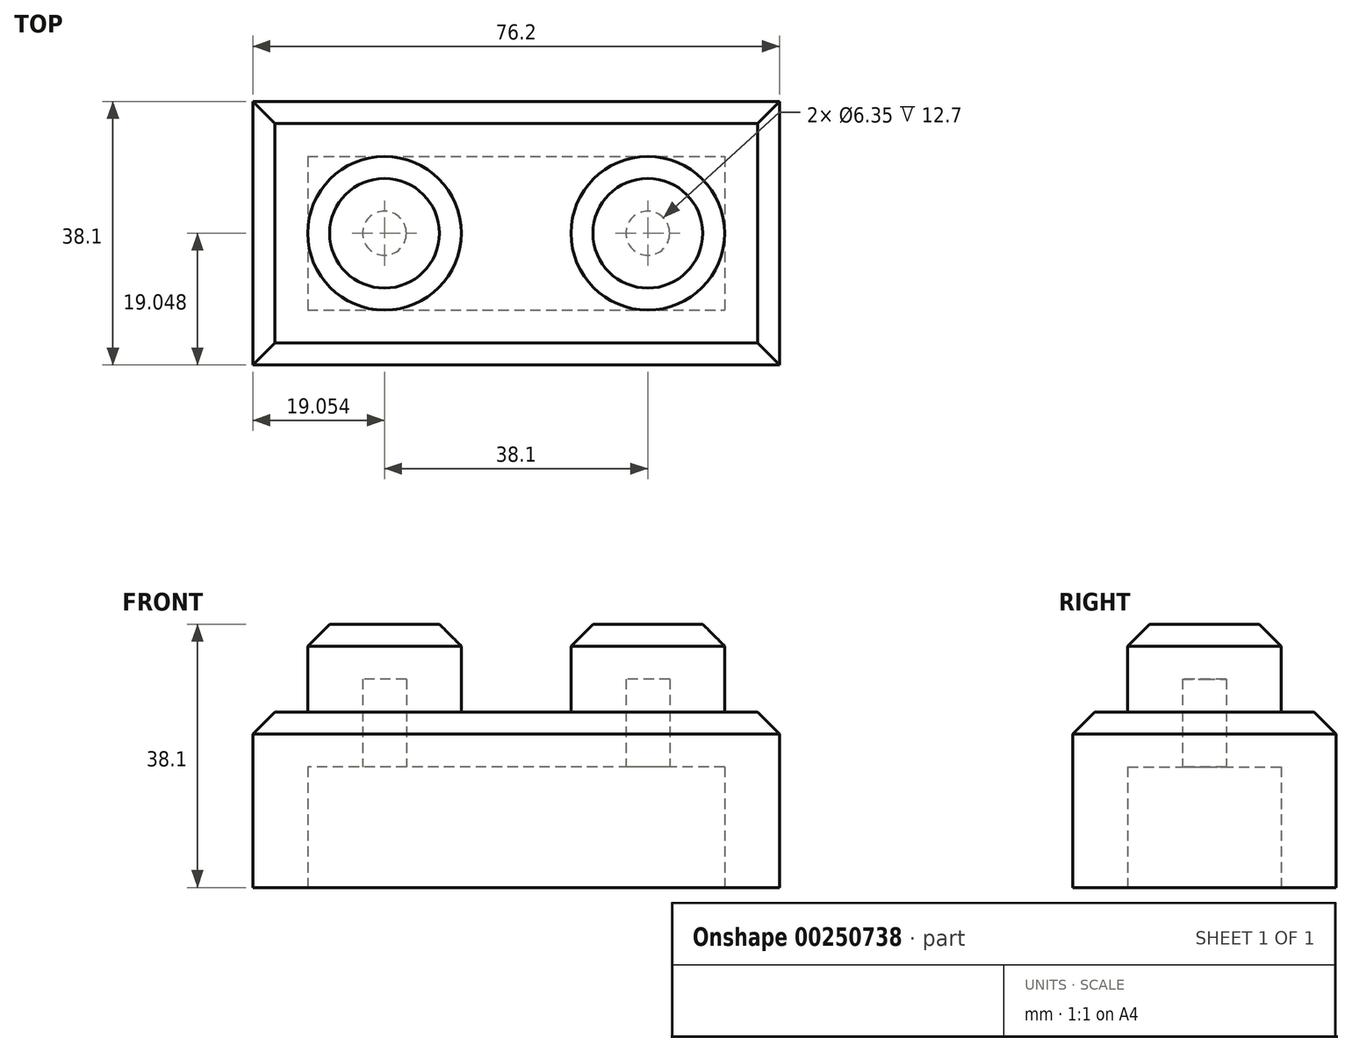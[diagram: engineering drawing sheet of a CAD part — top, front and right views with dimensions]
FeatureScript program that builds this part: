
annotation { "Feature Type Name" : "Feature", "Feature Type Description" : "" }
export const myFeature = defineFeature(function(context is Context, id is Id, definition is map)
    precondition{}
    {
        {
            var Q0;
            Q0=qCreatedBy(makeId("Top.planeOp"),FACE);
            var sketch = newSketch(context, id + "F0", { "sketchPlane" : qUnion([Q0])});
            skLineSegment(sketch, "E0.bottom", {"start": v(-12.45, 10.05) * mm, "end": v(63.75, 10.05) * mm});
            skLineSegment(sketch, "E0.top", {"start": v(-12.45, -28.05) * mm, "end": v(63.75, -28.05) * mm});
            skLineSegment(sketch, "E0.left", {"start": v(-12.45, 10.05) * mm, "end": v(-12.45, -28.05) * mm});
            skLineSegment(sketch, "E0.right", {"start": v(63.75, 10.05) * mm, "end": v(63.75, -28.05) * mm});
            skSolve(sketch);
        }
        {
            var Q0;
            Q0=makeQuery(id+"F0.imprint","IMPRINT",FACE,{"disambiguationData":[TD([[makeQuery(id+"F0.imprint","IMPRINT",EDGE,{"derivedFrom":sQuery(id+"F0.wireOp",EDGE,"E0.bottom")}),-1.0]])]});
            extrude(context, id + "F1", {"entities" : qUnion([Q0]), "depth" : 25.4 * mm});
        }
        {
            var Q0;
            Q0=makeQuery(id+"F1.opExtrude","CAP_FACE",FACE,{"disambiguationData":[OSD([sQuery(id+"F0.wireOp",EDGE,"E0.bottom"),sQuery(id+"F0.wireOp",EDGE,"E0.top"),sQuery(id+"F0.wireOp",EDGE,"E0.left"),sQuery(id+"F0.wireOp",EDGE,"E0.right")])],"isStart":false});
            var sketch = newSketch(context, id + "F2", { "sketchPlane" : qUnion([Q0])});
            skCircle(sketch, "E1", {"center": v(6.6, -9) * mm, "radius": 11.11 * mm});
            skPoint(sketch, "E1.centerSnap0", {"position": v(-12.45, -9) * mm});
            skCircle(sketch, "E2", {"center": v(44.7, -9) * mm, "radius": 11.11 * mm});
            skPoint(sketch, "E2.centerSnap0", {"position": v(63.75, -9) * mm});
            skSolve(sketch);
        }
        {
            var Q0;
            Q0 = qSketchRegion(id + "F2", true);
            extrude(context, id + "F3", {"entities" : qUnion([Q0]), "operationType" : NewBodyOperationType.ADD, "depth" : 12.7 * mm});
        }
        {
            var Q0;
            Q0=makeQuery(id+"F3.opExtrude","CAP_FACE",FACE,{"disambiguationData":[OSD([sQuery(id+"F2.wireOp",EDGE,"E1")])],"isStart":false});
            var Q1;
            Q1=makeQuery(id+"F3.opExtrude","CAP_FACE",FACE,{"disambiguationData":[OSD([sQuery(id+"F2.wireOp",EDGE,"E2")])],"isStart":false});
            var Q2;
            Q2=makeQuery(id+"F1.opExtrude","CAP_EDGE",EDGE,{"disambiguationData":[OSD([sQuery(id+"F0.wireOp",EDGE,"E0.left")])],"isStart":false});
            var Q3;
            Q3=makeQuery(id+"F1.opExtrude","CAP_EDGE",EDGE,{"disambiguationData":[OSD([sQuery(id+"F0.wireOp",EDGE,"E0.bottom")])],"isStart":false});
            var Q4;
            Q4=makeQuery(id+"F1.opExtrude","CAP_EDGE",EDGE,{"disambiguationData":[OSD([sQuery(id+"F0.wireOp",EDGE,"E0.top")])],"isStart":false});
            var Q5;
            Q5=makeQuery(id+"F1.opExtrude","CAP_EDGE",EDGE,{"disambiguationData":[OSD([sQuery(id+"F0.wireOp",EDGE,"E0.right")])],"isStart":false});
            chamfer(context, id + "F4", {"entities" : qUnion([Q0, Q1, Q2, Q3, Q4, Q5]), "width" : 3.17 * mm, "tangentPropagation" : true});
        }
        {
            var Q0;
            Q0=makeQuery(id+"F1.opExtrude","CAP_FACE",FACE,{"disambiguationData":[OSD([sQuery(id+"F0.wireOp",EDGE,"E0.bottom"),sQuery(id+"F0.wireOp",EDGE,"E0.top"),sQuery(id+"F0.wireOp",EDGE,"E0.left"),sQuery(id+"F0.wireOp",EDGE,"E0.right")])],"isStart":true});
            shell(context, id + "F5", {"entities" : qUnion([Q0]), "thickness" : 7.94 * mm});
        }
    });
